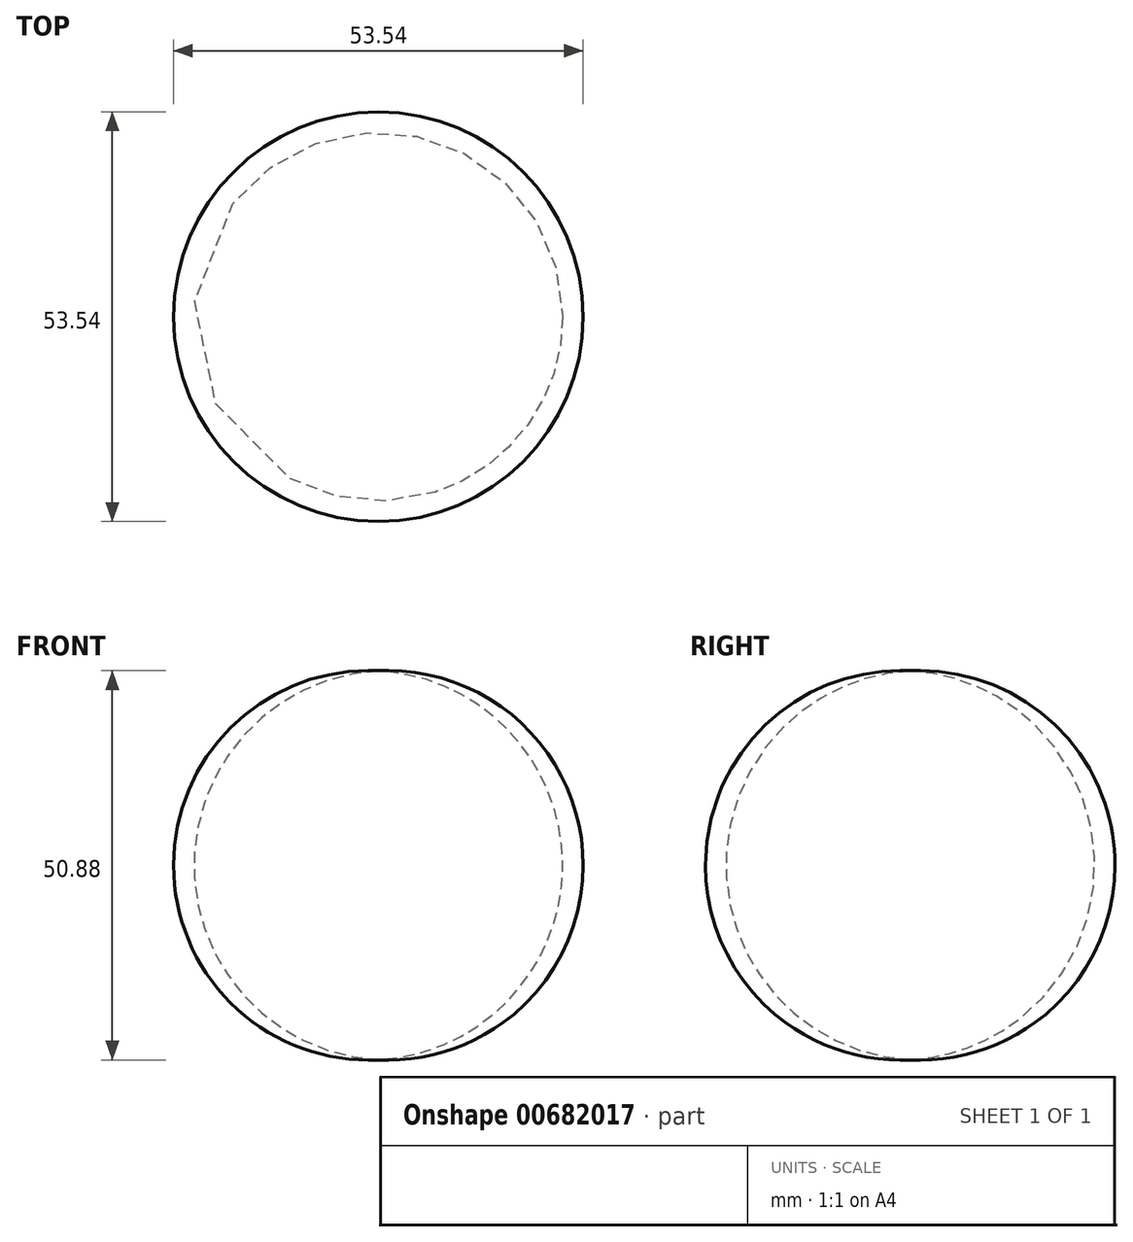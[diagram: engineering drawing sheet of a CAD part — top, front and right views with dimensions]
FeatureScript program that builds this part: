
annotation { "Feature Type Name" : "Feature", "Feature Type Description" : "" }
export const myFeature = defineFeature(function(context is Context, id is Id, definition is map)
    precondition{}
    {
        {
            var Q0;
            Q0=qCreatedBy(makeId("Front.planeOp"),FACE);
            var sketch = newSketch(context, id + "F0", { "sketchPlane" : qUnion([Q0])});
            skLineSegment(sketch, "E0", {"start": v(0, 0) * mm, "end": v(0, 50.8) * mm});
            skArc(sketch, "E1", {"start": v(0, 0) * mm, "mid": v(26.77, 25.4) * mm, "end": v(0, 50.8) * mm});
            skSolve(sketch);
        }
        {
            var Q0;
            Q0=makeQuery(id+"F0.imprint","IMPRINT",FACE,{"disambiguationData":[TD([[makeQuery(id+"F0.imprint","IMPRINT",EDGE,{"derivedFrom":sQuery(id+"F0.wireOp",EDGE,"E0")}),-1.0]])]});
            var Q1;
            Q1=sQuery(id+"F0.wireOp",EDGE,"E0");
            revolve(context, id + "F1", {"entities" : qUnion([Q0]), "axis" : qUnion([Q1]), "revolveType" : RevolveType.FULL});
        }
    });
